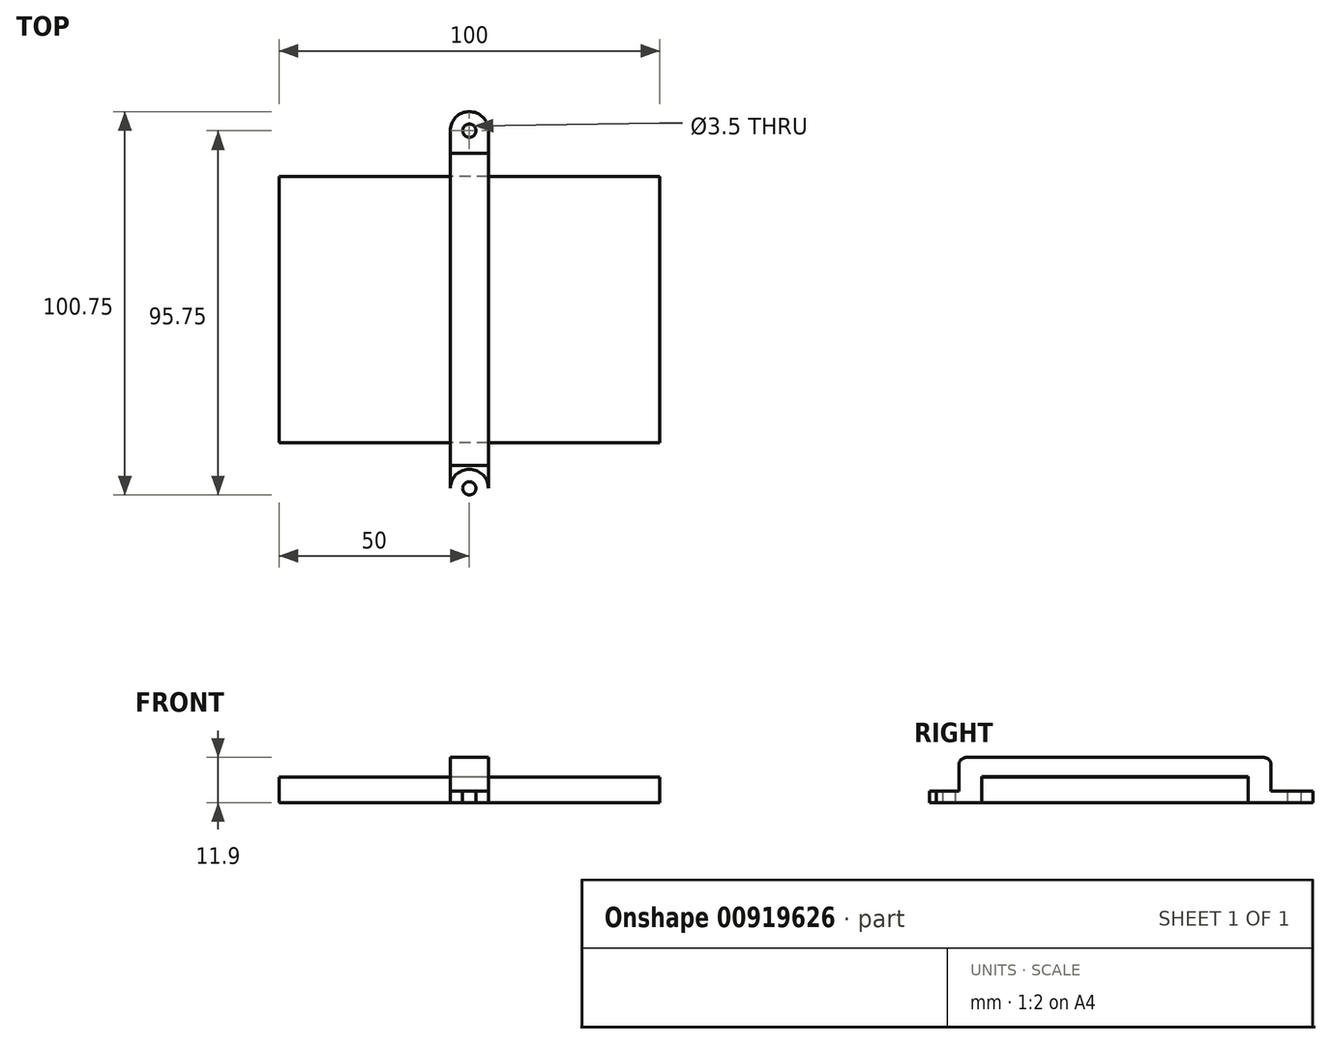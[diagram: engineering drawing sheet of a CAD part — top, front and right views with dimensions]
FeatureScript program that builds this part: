
annotation { "Feature Type Name" : "Feature", "Feature Type Description" : "" }
export const myFeature = defineFeature(function(context is Context, id is Id, definition is map)
    precondition{}
    {
        {
            var Q0;
            Q0=qCreatedBy(makeId("Top.planeOp"),FACE);
            var sketch = newSketch(context, id + "F0", { "sketchPlane" : qUnion([Q0])});
            skLineSegment(sketch, "E0.rect.bottom", {"start": v(50, -35) * mm, "end": v(-50, -35) * mm});
            skLineSegment(sketch, "E0.rect.top", {"start": v(50, 35) * mm, "end": v(-50, 35) * mm});
            skLineSegment(sketch, "E0.rect.left", {"start": v(50, -35) * mm, "end": v(50, 35) * mm});
            skLineSegment(sketch, "E0.rect.right", {"start": v(-50, -35) * mm, "end": v(-50, 35) * mm});
            skPoint(sketch, "E0.rect.middle", {"position": v(0, 0) * mm});
            skSolve(sketch);
        }
        {
            var Q0;
            Q0=qSketchRegion(id+"F0",true);
            extrude(context, id + "F1", {"entities" : qUnion([Q0]), "depth" : 6.7 * mm});
        }
        {
            var Q0;
            Q0=qCreatedBy(makeId("Top.planeOp"),FACE);
            var sketch = newSketch(context, id + "F2", { "sketchPlane" : qUnion([Q0])});
            skCircle(sketch, "E1", {"center": v(0, 47) * mm, "radius": 1.75 * mm});
            skCircle(sketch, "E2", {"center": v(0, 47) * mm, "radius": 5 * mm});
            skLineSegment(sketch, "E3.top", {"start": v(-5, 35) * mm, "end": v(5, 35) * mm});
            skLineSegment(sketch, "E3.left", {"start": v(-5, 47) * mm, "end": v(-5, 35) * mm});
            skLineSegment(sketch, "E3.right", {"start": v(5, 47) * mm, "end": v(5, 35) * mm});
            skLineSegment(sketch, "E4", {"start": v(-5, 41) * mm, "end": v(5, 41) * mm});
            skCircle(sketch, "E5.MirrorC", {"center": v(0, -47) * mm, "radius": 5 * mm});
            skCircle(sketch, "E6.MirrorC", {"center": v(0, -47) * mm, "radius": 1.75 * mm});
            skLineSegment(sketch, "E7.MirrorCS", {"start": v(-5, -47) * mm, "end": v(-5, -35) * mm});
            skLineSegment(sketch, "E8.MirrorCS", {"start": v(-5, -41) * mm, "end": v(5, -41) * mm});
            skLineSegment(sketch, "E9.MirrorCS", {"start": v(5, -47) * mm, "end": v(5, -35) * mm});
            skLineSegment(sketch, "E10.MirrorCS", {"start": v(-5, -35) * mm, "end": v(5, -35) * mm});
            skSolve(sketch);
        }
        {
            var Q0;
            Q0=makeQuery(id+"F2.imprint","IMPRINT",FACE,{"disambiguationData":[TD([[makeQuery(id+"F2.imprint","IMPRINT",EDGE,{"derivedFrom":sQuery(id+"F2.wireOp",EDGE,"E1")}),-1.0]])]});
            var Q1;
            {var subQ1=sQuery(id+"F2.wireOp",EDGE,"E4");Q1=makeQuery(id+"F2.imprint","IMPRINT",FACE,{"disambiguationData":[TD([[makeQuery(id+"F2.imprint","IMPRINT",EDGE,{"derivedFrom":subQ1}),1.0]])]});}
            var Q2;
            Q2=makeQuery(id+"F2.imprint","IMPRINT",FACE,{"disambiguationData":[TD([[makeQuery(id+"F2.imprint","IMPRINT",EDGE,{"derivedFrom":sQuery(id+"F2.wireOp",EDGE,"E6.MirrorC")}),1.0]])]});
            var Q3;
            {var subQ3=sQuery(id+"F2.wireOp",EDGE,"E8.MirrorCS");Q3=makeQuery(id+"F2.imprint","IMPRINT",FACE,{"disambiguationData":[TD([[makeQuery(id+"F2.imprint","IMPRINT",EDGE,{"derivedFrom":subQ3}),-1.0]])]});}
            extrude(context, id + "F3", {"entities" : qUnion([Q0, Q1, Q2, Q3]), "depth" : 3 * mm});
        }
        {
            var Q0;
            {var subQ2=sQuery(id+"F2.wireOp",EDGE,"E3.top");Q0=makeQuery(id+"F2.imprint","IMPRINT",FACE,{"disambiguationData":[TD([[makeQuery(id+"F2.imprint","IMPRINT",EDGE,{"derivedFrom":subQ2}),1.0]])]});}
            var Q1;
            {var subQ2=sQuery(id+"F2.wireOp",EDGE,"E8.MirrorCS");Q1=makeQuery(id+"F2.imprint","IMPRINT",FACE,{"disambiguationData":[TD([[makeQuery(id+"F2.imprint","IMPRINT",EDGE,{"derivedFrom":subQ2}),1.0]])]});}
            extrude(context, id + "F4", {"entities" : qUnion([Q0, Q1]), "operationType" : NewBodyOperationType.ADD, "depth" : 6.9 * mm});
        }
        {
            var Q0;
            Q0=makeQuery(id+"F4.opExtrude","CAP_FACE",FACE,{"disambiguationData":[OSD([sQuery(id+"F2.wireOp",EDGE,"E3.top"),sQuery(id+"F2.wireOp",EDGE,"E3.left"),sQuery(id+"F2.wireOp",EDGE,"E3.right"),sQuery(id+"F2.wireOp",EDGE,"E4")])],"isStart":false});
            var sketch = newSketch(context, id + "F5", { "sketchPlane" : qUnion([Q0])});
            skLineSegment(sketch, "E11.bottom", {"start": v(-5, 41) * mm, "end": v(5, 41) * mm});
            skLineSegment(sketch, "E11.top", {"start": v(-5, -41) * mm, "end": v(5, -41) * mm});
            skLineSegment(sketch, "E11.left", {"start": v(-5, 41) * mm, "end": v(-5, -41) * mm});
            skLineSegment(sketch, "E11.right", {"start": v(5, 41) * mm, "end": v(5, -41) * mm});
            skSolve(sketch);
        }
        {
            var Q0;
            Q0=qSketchRegion(id+"F5",true);
            extrude(context, id + "F6", {"entities" : qUnion([Q0]), "operationType" : NewBodyOperationType.ADD, "depth" : 5 * mm});
        }
        {
            var Q0;
            Q0=makeQuery(id+"F6.opExtrude","CAP_EDGE",EDGE,{"disambiguationData":[OSD([sQuery(id+"F5.wireOp",EDGE,"E11.bottom")])],"isStart":false});
            var Q1;
            Q1=makeQuery(id+"F6.opExtrude","CAP_EDGE",EDGE,{"disambiguationData":[OSD([sQuery(id+"F5.wireOp",EDGE,"E11.top")])],"isStart":false});
            var Q2;
            Q2=makeQuery(id+"F3.opExtrude","CAP_EDGE",EDGE,{"disambiguationData":[OSD([sQuery(id+"F2.wireOp",EDGE,"E8.MirrorCS")])],"isStart":false});
            var Q3;
            Q3=makeQuery(id+"F3.opExtrude","CAP_EDGE",EDGE,{"disambiguationData":[OSD([sQuery(id+"F2.wireOp",EDGE,"E4")])],"isStart":false});
            fillet(context, id + "F7", {"entities" : qUnion([Q0, Q1, Q2, Q3]), "radius" : 2 * mm, "tangentPropagation" : true, "allowEdgeOverflow" : false});
        }
    });
